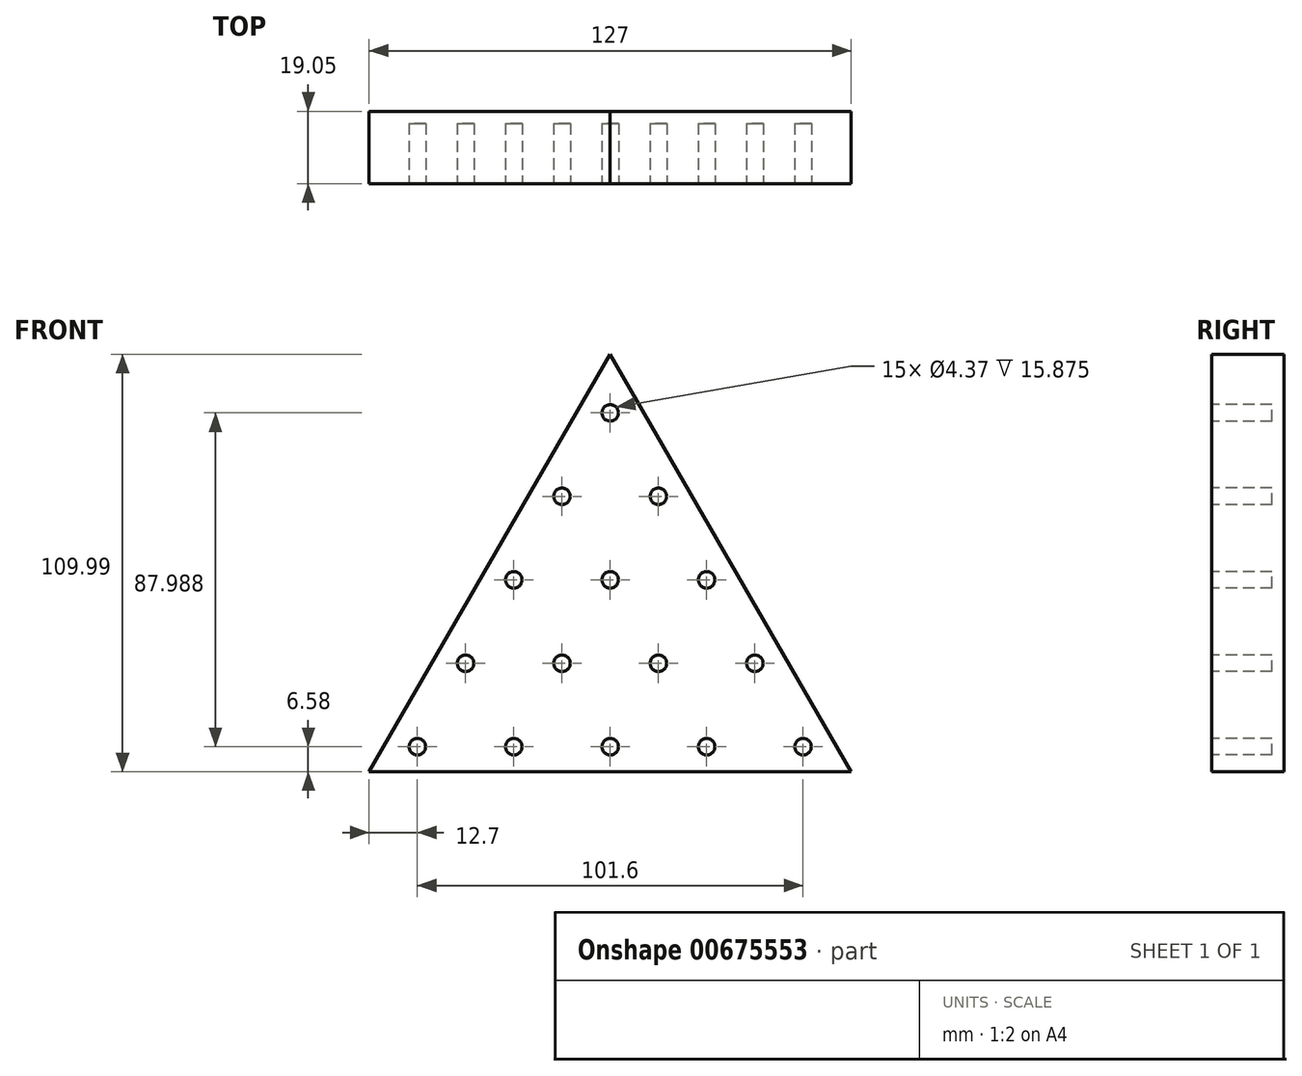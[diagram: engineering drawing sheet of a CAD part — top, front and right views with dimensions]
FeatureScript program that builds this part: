
annotation { "Feature Type Name" : "Feature", "Feature Type Description" : "" }
export const myFeature = defineFeature(function(context is Context, id is Id, definition is map)
    precondition{}
    {
        {
            var Q0;
            Q0=qCreatedBy(makeId("Front.planeOp"),FACE);
            var sketch = newSketch(context, id + "F0", { "sketchPlane" : qUnion([Q0])});
            skLineSegment(sketch, "E0", {"start": v(0, 109.99) * mm, "end": v(-63.5, 0) * mm});
            skLineSegment(sketch, "E1", {"start": v(-63.5, 0) * mm, "end": v(63.5, 0) * mm});
            skLineSegment(sketch, "E2", {"start": v(63.5, 0) * mm, "end": v(0, 109.99) * mm});
            skSolve(sketch);
        }
        {
            var Q0;
            Q0=makeQuery(id+"F0.imprint","IMPRINT",FACE,{"disambiguationData":[TD([[makeQuery(id+"F0.imprint","IMPRINT",EDGE,{"derivedFrom":sQuery(id+"F0.wireOp",EDGE,"E0")}),1.0]])]});
            extrude(context, id + "F1", {"entities" : qUnion([Q0]), "depth" : 19.05 * mm, "offsetDistance" : 25.4 * mm});
        }
        {
            var Q0;
            Q0=makeQuery(id+"F1.opExtrude","CAP_FACE",FACE,{"disambiguationData":[OSD([sQuery(id+"F0.wireOp",EDGE,"E0"),sQuery(id+"F0.wireOp",EDGE,"E1"),sQuery(id+"F0.wireOp",EDGE,"E2")])],"isStart":false});
            var sketch = newSketch(context, id + "F2", { "sketchPlane" : qUnion([Q0])});
            skCircle(sketch, "E3", {"center": v(0, 94.57) * mm, "radius": 2.18 * mm});
            skCircle(sketch, "E4", {"center": v(-12.7, 72.57) * mm, "radius": 2.18 * mm});
            skCircle(sketch, "E5", {"center": v(-25.4, 50.57) * mm, "radius": 2.18 * mm});
            skCircle(sketch, "E6", {"center": v(-38.1, 28.58) * mm, "radius": 2.18 * mm});
            skCircle(sketch, "E7", {"center": v(-50.8, 6.58) * mm, "radius": 2.18 * mm});
            skCircle(sketch, "E8", {"center": v(12.7, 72.57) * mm, "radius": 2.18 * mm});
            skCircle(sketch, "E9", {"center": v(25.4, 50.57) * mm, "radius": 2.18 * mm});
            skCircle(sketch, "E10", {"center": v(0, 50.57) * mm, "radius": 2.18 * mm});
            skCircle(sketch, "E11", {"center": v(-12.7, 28.58) * mm, "radius": 2.18 * mm});
            skCircle(sketch, "E12", {"center": v(12.7, 28.58) * mm, "radius": 2.18 * mm});
            skCircle(sketch, "E13", {"center": v(38.1, 28.58) * mm, "radius": 2.18 * mm});
            skCircle(sketch, "E14", {"center": v(-25.4, 6.58) * mm, "radius": 2.18 * mm});
            skCircle(sketch, "E15", {"center": v(0, 6.58) * mm, "radius": 2.18 * mm});
            skCircle(sketch, "E16", {"center": v(25.4, 6.58) * mm, "radius": 2.18 * mm});
            skCircle(sketch, "E17", {"center": v(50.8, 6.58) * mm, "radius": 2.18 * mm});
            skSolve(sketch);
        }
        {
            var Q0;
            Q0 = qSketchRegion(id + "F2", true);
            extrude(context, id + "F3", {"entities" : qUnion([Q0]), "operationType" : NewBodyOperationType.REMOVE, "oppositeDirection" : true, "depth" : 15.88 * mm, "offsetDistance" : 25.4 * mm});
        }
    });
